# Revit family: Extension baying kit Linkeo
name_source: partatom
category: Equipement spécialisé
units: mm (PartAtom-declared; Revit-internal decimal feet)

## family parameters
Basée sur le plan de construction = Non
Cote de connecteur circulaire = Utiliser le diamètre
Couper avec des vides une fois chargée = Non
Numéro OmniClass = 23.85.05.17.11.14
Partagée = Oui
Point de calcul de pièce = Non
Titre OmniClass = Multimedia Broadcasting Equipment
Toujours verticalement = Oui
Type d'élément = Normal

## types (1)
- Extension for cabinet Linkeo2 42U 800x800
    Application class = EC002499
    Avec porte frontale = Oui
    BIM wording = Cabinet Linkeo2 42U 800x800
    Color = grey
    Degree of protection IK = IK08
    Degree of protection IP = IP20
    Depth = 830 mm  [stored 2.7231 ft]
    Depth of the model (mm) = 800 mm  [stored 2.62467 ft]
    Distance of the aperture 1 = 257 mm  [stored 0.843176 ft]
    Distance of the aperture 2 = 198 mm  [stored 0.649606 ft]
    Door symbol = Door symbol  Door 800mm
    E-catalogue link = https://www.legrand.fr
    EAN = 3414971001633
    Elévation par défaut = 0 mm  [stored 0 ft]
    Fabricant = Legrand
    Front door material = glass
    Function = Cabinet Linkeo2
    Height = 2026 mm  [stored 6.64698 ft]
    Legrand part number = 646770
    Locking of the front door = One point
    Material = Steel
    Max load capacity = 400
    Model = With permanent frame
    Model width = 800 mm  [stored 2.62467 ft]
    Modular spacing = 19 inches
    Mounting level = Front side
    Number of doors = 1
    Number of height units = 42
    Operating temperature = -25°C à 70°C
    RAL Number = 7016
    Rack location = 93 mm  [stored 0.305118 ft]
    Storage temperature = -25°C à 70°C
    Type of horizontal uprights = Horizontal uprights for Linkeo freestanding cabinets  42U depth 800
    Type of levelling feet = Levelling feet  800X800
    Type of profile rail = Crank
    Type of surface = Powder coating
    Type of ventilation = None
    Type of vertical uprights = Vertical uprights for Linkeo freestanding cabinets  42U
    Usable height (mm) = 1786 mm  [stored 5.85958 ft]
    Usable width (mm) = 690 mm  [stored 2.26378 ft]
    Width (mm) = 810 mm
    With earthing = Oui
    With roof plate = Oui

note: [stored X ft] marks values corroborated as IEEE doubles in the binary element streams (Revit-internal decimal feet)
